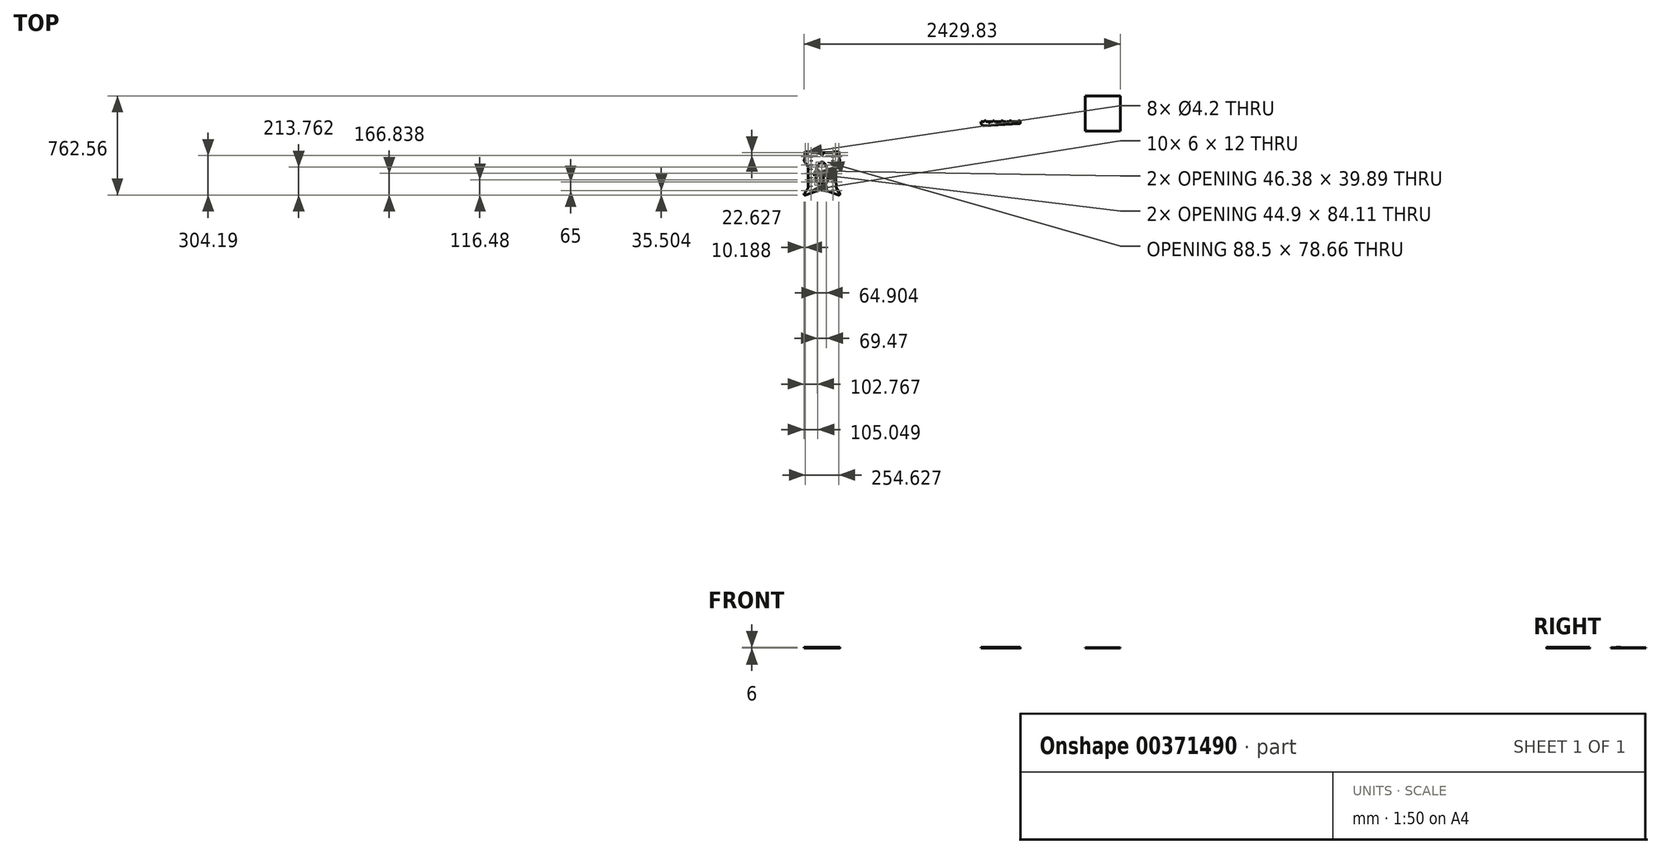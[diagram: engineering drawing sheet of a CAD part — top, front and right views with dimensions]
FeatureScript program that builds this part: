
annotation { "Feature Type Name" : "Feature", "Feature Type Description" : "" }
export const myFeature = defineFeature(function(context is Context, id is Id, definition is map)
    precondition{}
    {
        {
            var Q0;
            Q0=qCreatedBy(makeId("Top.planeOp"),FACE);
            var sketch = newSketch(context, id + "F0", { "sketchPlane" : qUnion([Q0])});
            skCircle(sketch, "E0", {"center": v(-43.53, 80.15) * mm, "radius": 6.15 * mm});
            skCircle(sketch, "E1", {"center": v(72.47, 79.15) * mm, "radius": 5.05 * mm});
            skLineSegment(sketch, "E2.bottom", {"start": v(-57.57, 96.15) * mm, "end": v(-15.53, 96.15) * mm});
            skLineSegment(sketch, "E2.left", {"start": v(-59.57, 94.15) * mm, "end": v(-59.57, 62.7) * mm});
            skLineSegment(sketch, "E2.right", {"start": v(204.43, 94.15) * mm, "end": v(204.43, 62.7) * mm});
            skCircle(sketch, "E3", {"center": v(-32.22, 91.47) * mm, "radius": 2.1 * mm});
            skCircle(sketch, "E4", {"center": v(-54.84, 91.47) * mm, "radius": 2.1 * mm});
            skCircle(sketch, "E5", {"center": v(-54.84, 68.84) * mm, "radius": 2.1 * mm});
            skCircle(sketch, "E6", {"center": v(-32.22, 68.84) * mm, "radius": 2.1 * mm});
            skCircle(sketch, "E7.1.0.0", {"center": v(188.47, 80.15) * mm, "radius": 6.15 * mm});
            skCircle(sketch, "E7.1.0.1", {"center": v(199.78, 91.47) * mm, "radius": 2.1 * mm});
            skCircle(sketch, "E7.1.0.2", {"center": v(177.16, 91.47) * mm, "radius": 2.1 * mm});
            skCircle(sketch, "E7.1.0.3", {"center": v(177.16, 68.84) * mm, "radius": 2.1 * mm});
            skCircle(sketch, "E7.1.0.4", {"center": v(199.78, 68.84) * mm, "radius": 2.1 * mm});
            skLineSegment(sketch, "E7.direction1", {"start": v(-43.53, 80.15) * mm, "end": v(188.47, 80.15) * mm, "construction": true});
            skCircle(sketch, "E8", {"center": v(72.47, 71.15) * mm, "radius": 1.65 * mm});
            skCircle(sketch, "E9", {"center": v(80.47, 79.15) * mm, "radius": 1.65 * mm});
            skCircle(sketch, "E10", {"center": v(72.47, 87.15) * mm, "radius": 1.65 * mm});
            skCircle(sketch, "E11", {"center": v(64.47, 79.15) * mm, "radius": 1.65 * mm});
            skLineSegment(sketch, "E12.bottom", {"start": v(-13.53, 86.15) * mm, "end": v(-7.53, 86.15) * mm});
            skLineSegment(sketch, "E12.top", {"start": v(-13.53, 74.15) * mm, "end": v(-7.53, 74.15) * mm});
            skLineSegment(sketch, "E12.left", {"start": v(-13.53, 86.15) * mm, "end": v(-13.53, 74.15) * mm});
            skLineSegment(sketch, "E12.right", {"start": v(-7.53, 86.15) * mm, "end": v(-7.53, 74.15) * mm});
            skLineSegment(sketch, "E13.0.1.0", {"start": v(-13.53, 21.15) * mm, "end": v(-7.53, 21.15) * mm});
            skLineSegment(sketch, "E13.0.1.1", {"start": v(-13.53, 21.15) * mm, "end": v(-13.53, 9.15) * mm});
            skLineSegment(sketch, "E13.0.1.2", {"start": v(-13.53, 9.15) * mm, "end": v(-7.53, 9.15) * mm});
            skLineSegment(sketch, "E13.0.1.3", {"start": v(-7.53, 21.15) * mm, "end": v(-7.53, 9.15) * mm});
            skLineSegment(sketch, "E13.0.2.0", {"start": v(-13.53, -43.85) * mm, "end": v(-7.53, -43.85) * mm});
            skLineSegment(sketch, "E13.0.2.1", {"start": v(-13.53, -43.85) * mm, "end": v(-13.53, -55.85) * mm});
            skLineSegment(sketch, "E13.0.2.2", {"start": v(-13.53, -55.85) * mm, "end": v(-7.53, -55.85) * mm});
            skLineSegment(sketch, "E13.0.2.3", {"start": v(-7.53, -43.85) * mm, "end": v(-7.53, -55.85) * mm});
            skLineSegment(sketch, "E13.0.3.0", {"start": v(-13.53, -108.85) * mm, "end": v(-7.53, -108.85) * mm});
            skLineSegment(sketch, "E13.0.3.1", {"start": v(-13.53, -108.85) * mm, "end": v(-13.53, -120.85) * mm});
            skLineSegment(sketch, "E13.0.3.2", {"start": v(-13.53, -120.85) * mm, "end": v(-7.53, -120.85) * mm});
            skLineSegment(sketch, "E13.0.3.3", {"start": v(-7.53, -108.85) * mm, "end": v(-7.53, -120.85) * mm});
            skLineSegment(sketch, "E13.1.0.0", {"start": v(152.47, 86.15) * mm, "end": v(158.47, 86.15) * mm});
            skLineSegment(sketch, "E13.1.0.1", {"start": v(152.47, 86.15) * mm, "end": v(152.47, 74.15) * mm});
            skLineSegment(sketch, "E13.1.0.2", {"start": v(152.47, 74.15) * mm, "end": v(158.47, 74.15) * mm});
            skLineSegment(sketch, "E13.1.0.3", {"start": v(158.47, 86.15) * mm, "end": v(158.47, 74.15) * mm});
            skLineSegment(sketch, "E13.1.1.0", {"start": v(152.47, 21.15) * mm, "end": v(158.47, 21.15) * mm});
            skLineSegment(sketch, "E13.1.1.1", {"start": v(152.47, 21.15) * mm, "end": v(152.47, 9.15) * mm});
            skLineSegment(sketch, "E13.1.1.2", {"start": v(152.47, 9.15) * mm, "end": v(158.47, 9.15) * mm});
            skLineSegment(sketch, "E13.1.1.3", {"start": v(158.47, 21.15) * mm, "end": v(158.47, 9.15) * mm});
            skLineSegment(sketch, "E13.1.2.0", {"start": v(152.47, -43.85) * mm, "end": v(158.47, -43.85) * mm});
            skLineSegment(sketch, "E13.1.2.1", {"start": v(152.47, -43.85) * mm, "end": v(152.47, -55.85) * mm});
            skLineSegment(sketch, "E13.1.2.2", {"start": v(152.47, -55.85) * mm, "end": v(158.47, -55.85) * mm});
            skLineSegment(sketch, "E13.1.2.3", {"start": v(158.47, -43.85) * mm, "end": v(158.47, -55.85) * mm});
            skLineSegment(sketch, "E13.1.3.0", {"start": v(152.47, -108.85) * mm, "end": v(158.47, -108.85) * mm});
            skLineSegment(sketch, "E13.1.3.1", {"start": v(152.47, -108.85) * mm, "end": v(152.47, -120.85) * mm});
            skLineSegment(sketch, "E13.1.3.2", {"start": v(152.47, -120.85) * mm, "end": v(158.47, -120.85) * mm});
            skLineSegment(sketch, "E13.1.3.3", {"start": v(158.47, -108.85) * mm, "end": v(158.47, -120.85) * mm});
            skLineSegment(sketch, "E13.direction1", {"start": v(-13.53, 86.15) * mm, "end": v(152.47, 86.15) * mm, "construction": true});
            skLineSegment(sketch, "E13.direction2", {"start": v(-13.53, 86.15) * mm, "end": v(-13.53, 21.15) * mm, "construction": true});
            skCircle(sketch, "E14", {"center": v(-10.53, 47.65) * mm, "radius": 2 * mm});
            skPoint(sketch, "E14.centerSnap0", {"position": v(-10.53, 74.15) * mm});
            skCircle(sketch, "E15.0.1.0", {"center": v(-10.53, -17.35) * mm, "radius": 2 * mm});
            skCircle(sketch, "E15.0.2.0", {"center": v(-10.53, -82.35) * mm, "radius": 2 * mm});
            skCircle(sketch, "E15.1.0.0", {"center": v(155.47, 47.65) * mm, "radius": 2 * mm});
            skCircle(sketch, "E15.1.1.0", {"center": v(155.47, -17.35) * mm, "radius": 2 * mm});
            skCircle(sketch, "E15.1.2.0", {"center": v(155.47, -82.35) * mm, "radius": 2 * mm});
            skLineSegment(sketch, "E15.direction1", {"start": v(-10.53, 47.65) * mm, "end": v(155.47, 47.65) * mm, "construction": true});
            skLineSegment(sketch, "E15.direction2", {"start": v(-10.53, 47.65) * mm, "end": v(-10.53, -17.35) * mm, "construction": true});
            skArc(sketch, "E16", {"start": v(23.68, -28.57) * mm, "mid": v(15.8, -47.74) * mm, "end": v(15.16, -68.46) * mm});
            skPoint(sketch, "E16.centerSnap0", {"position": v(72.47, 47.65) * mm});
            skArc(sketch, "E17", {"start": v(95.76, 21.5) * mm, "mid": v(72.47, 37.74) * mm, "end": v(49.18, 21.5) * mm});
            skArc(sketch, "E18", {"start": v(38.9, -121.45) * mm, "mid": v(48.6, -133.7) * mm, "end": v(62.47, -140.92) * mm});
            skLineSegment(sketch, "E19", {"start": v(17.57, -78.4) * mm, "end": v(38.9, -121.45) * mm});
            skLineSegment(sketch, "E20", {"start": v(106.05, -121.45) * mm, "end": v(127.37, -78.4) * mm});
            skArc(sketch, "E21.trimOffspring", {"start": v(129.78, -68.46) * mm, "mid": v(129.14, -47.74) * mm, "end": v(121.26, -28.57) * mm});
            skLineSegment(sketch, "E22", {"start": v(28.22, -19.65) * mm, "end": v(49.18, 21.5) * mm});
            skLineSegment(sketch, "E23", {"start": v(95.76, 21.5) * mm, "end": v(116.72, -19.65) * mm});
            skLineSegment(sketch, "E24.top", {"start": v(-11.53, 91.15) * mm, "end": v(156.47, 91.15) * mm});
            skLineSegment(sketch, "E24.left", {"start": v(-13.53, 94.15) * mm, "end": v(-13.53, 93.15) * mm});
            skLineSegment(sketch, "E24.right", {"start": v(158.47, 94.15) * mm, "end": v(158.47, 93.15) * mm});
            skLineSegment(sketch, "E25.trimOffspring", {"start": v(160.47, 96.15) * mm, "end": v(202.43, 96.15) * mm});
            skPoint(sketch, "E26.visualSharp", {"position": v(-13.53, 96.15) * mm});
            skArc(sketch, "E26.filletArc", {"start": v(-13.53, 94.15) * mm, "mid": v(-14.12, 95.57) * mm, "end": v(-15.53, 96.15) * mm});
            skPoint(sketch, "E27.visualSharp", {"position": v(-13.53, 91.15) * mm});
            skArc(sketch, "E27.filletArc", {"start": v(-13.53, 93.15) * mm, "mid": v(-12.94, 91.74) * mm, "end": v(-11.53, 91.15) * mm});
            skPoint(sketch, "E28.visualSharp", {"position": v(158.47, 96.15) * mm});
            skArc(sketch, "E28.filletArc", {"start": v(160.47, 96.15) * mm, "mid": v(159.06, 95.57) * mm, "end": v(158.47, 94.15) * mm});
            skPoint(sketch, "E29.visualSharp", {"position": v(158.47, 91.15) * mm});
            skArc(sketch, "E29.filletArc", {"start": v(156.47, 91.15) * mm, "mid": v(157.88, 91.74) * mm, "end": v(158.47, 93.15) * mm});
            skPoint(sketch, "E30.visualSharp", {"position": v(204.43, 96.15) * mm});
            skArc(sketch, "E30.filletArc", {"start": v(204.43, 94.15) * mm, "mid": v(203.84, 95.57) * mm, "end": v(202.43, 96.15) * mm});
            skPoint(sketch, "E31.visualSharp", {"position": v(-59.57, 96.15) * mm});
            skArc(sketch, "E31.filletArc", {"start": v(-57.57, 96.15) * mm, "mid": v(-58.98, 95.57) * mm, "end": v(-59.57, 94.15) * mm});
            skCircle(sketch, "E32", {"center": v(-57.53, -207.85) * mm, "radius": 2.5 * mm});
            skPoint(sketch, "E32.centerSnap0", {"position": v(-10.53, -120.85) * mm});
            skCircle(sketch, "E33", {"center": v(202.47, -207.85) * mm, "radius": 2.5 * mm});
            skCircle(sketch, "E34", {"center": v(-57.53, 52.15) * mm, "radius": 2.5 * mm});
            skCircle(sketch, "E35", {"center": v(202.47, 52.15) * mm, "radius": 2.5 * mm});
            skArc(sketch, "E36", {"start": v(208.74, 48.03) * mm, "mid": v(209.97, 52.18) * mm, "end": v(208.7, 56.33) * mm});
            skLineSegment(sketch, "E37", {"start": v(204.43, 62.7) * mm, "end": v(208.7, 56.33) * mm});
            skArc(sketch, "E38", {"start": v(-63.53, -203.35) * mm, "mid": v(-63.6, -212.27) * mm, "end": v(-55.09, -214.94) * mm});
            skArc(sketch, "E39", {"start": v(200.03, -214.94) * mm, "mid": v(208.35, -212.5) * mm, "end": v(208.8, -203.84) * mm});
            skArc(sketch, "E40", {"start": v(-63.8, 56.27) * mm, "mid": v(-65.03, 52.15) * mm, "end": v(-63.8, 48.03) * mm});
            skLineSegment(sketch, "E41", {"start": v(-59.57, 62.7) * mm, "end": v(-63.8, 56.27) * mm});
            skLineSegment(sketch, "E42", {"start": v(-63.8, 48.03) * mm, "end": v(-38.8, 10) * mm});
            skLineSegment(sketch, "E43", {"start": v(-32.22, -11.97) * mm, "end": v(-32.22, -148.25) * mm});
            skLineSegment(sketch, "E44", {"start": v(-40.21, -172.24) * mm, "end": v(-63.8, -203.7) * mm});
            skLineSegment(sketch, "E45", {"start": v(208.74, 48.03) * mm, "end": v(184.1, 10.56) * mm});
            skLineSegment(sketch, "E46", {"start": v(177.54, -12.63) * mm, "end": v(182.09, -161.58) * mm});
            skLineSegment(sketch, "E47", {"start": v(182.09, -161.58) * mm, "end": v(208.8, -203.84) * mm});
            skLineSegment(sketch, "E48", {"start": v(-55.09, -214.94) * mm, "end": v(59.43, -175.45) * mm});
            skLineSegment(sketch, "E49", {"start": v(85.5, -175.45) * mm, "end": v(200.03, -214.94) * mm});
            skLineSegment(sketch, "E50", {"start": v(23.68, -28.57) * mm, "end": v(60.93, -46.47) * mm});
            skLineSegment(sketch, "E51", {"start": v(17.57, -78.4) * mm, "end": v(62.47, -56.82) * mm});
            skLineSegment(sketch, "E52", {"start": v(28.22, -19.65) * mm, "end": v(72.47, -40.92) * mm});
            skLineSegment(sketch, "E53", {"start": v(116.72, -19.65) * mm, "end": v(72.47, -40.92) * mm});
            skLineSegment(sketch, "E54.trimOffspring", {"start": v(84.01, -46.47) * mm, "end": v(129.78, -68.46) * mm});
            skLineSegment(sketch, "E55.trimOffspring", {"start": v(60.93, -46.47) * mm, "end": v(15.16, -68.46) * mm});
            skLineSegment(sketch, "E56.trimOffspring", {"start": v(82.47, -56.82) * mm, "end": v(127.37, -78.4) * mm});
            skLineSegment(sketch, "E57.trimOffspring", {"start": v(84.01, -46.47) * mm, "end": v(121.26, -28.57) * mm});
            skLineSegment(sketch, "E58.left", {"start": v(62.47, -56.82) * mm, "end": v(62.47, -140.92) * mm});
            skLineSegment(sketch, "E58.right", {"start": v(82.47, -56.82) * mm, "end": v(82.47, -140.92) * mm});
            skLineSegment(sketch, "E59.0.0.4", {"start": v(-13.53, -173.85) * mm, "end": v(-7.53, -173.85) * mm});
            skLineSegment(sketch, "E59.3.0.4", {"start": v(-13.53, -173.85) * mm, "end": v(-13.53, -185.85) * mm});
            skLineSegment(sketch, "E59.6.0.4", {"start": v(-13.53, -185.85) * mm, "end": v(-7.53, -185.85) * mm});
            skLineSegment(sketch, "E59.9.0.4", {"start": v(-7.53, -173.85) * mm, "end": v(-7.53, -185.85) * mm});
            skLineSegment(sketch, "E59.0.1.4", {"start": v(152.47, -173.85) * mm, "end": v(158.47, -173.85) * mm});
            skLineSegment(sketch, "E59.3.1.4", {"start": v(152.47, -173.85) * mm, "end": v(152.47, -185.85) * mm});
            skLineSegment(sketch, "E59.6.1.4", {"start": v(152.47, -185.85) * mm, "end": v(158.47, -185.85) * mm});
            skLineSegment(sketch, "E59.9.1.4", {"start": v(158.47, -173.85) * mm, "end": v(158.47, -185.85) * mm});
            skCircle(sketch, "E60.0.0.3", {"center": v(-10.53, -147.35) * mm, "radius": 2 * mm});
            skCircle(sketch, "E60.0.1.3", {"center": v(155.47, -147.35) * mm, "radius": 2 * mm});
            skPoint(sketch, "E61.orphan", {"position": v(72.47, -52.01) * mm});
            skArc(sketch, "E62.trimOffspring", {"start": v(82.47, -140.92) * mm, "mid": v(96.33, -133.7) * mm, "end": v(106.05, -121.45) * mm});
            skPoint(sketch, "E63.visualSharp", {"position": v(72.47, -170.96) * mm});
            skArc(sketch, "E63.filletArc", {"start": v(85.5, -175.45) * mm, "mid": v(72.47, -173.27) * mm, "end": v(59.43, -175.45) * mm});
            skPoint(sketch, "E64.visualSharp", {"position": v(-32.22, -161.58) * mm});
            skArc(sketch, "E64.filletArc", {"start": v(-40.21, -172.24) * mm, "mid": v(-34.27, -160.9) * mm, "end": v(-32.22, -148.25) * mm});
            skPoint(sketch, "E65.visualSharp", {"position": v(177.16, 0) * mm});
            skArc(sketch, "E65.filletArc", {"start": v(184.1, 10.56) * mm, "mid": v(179.03, -0.53) * mm, "end": v(177.54, -12.63) * mm});
            skPoint(sketch, "E66.visualSharp", {"position": v(-32.22, 0) * mm});
            skArc(sketch, "E66.filletArc", {"start": v(-32.22, -11.97) * mm, "mid": v(-33.9, -0.5) * mm, "end": v(-38.8, 10) * mm});
            skLineSegment(sketch, "E67.top", {"start": v(-1752.05, -335.9) * mm, "end": v(-1746.05, -335.9) * mm});
            skLineSegment(sketch, "E67.right", {"start": v(-1746.05, -323.9) * mm, "end": v(-1746.05, -335.9) * mm});
            skLineSegment(sketch, "E68.0.1.0", {"start": v(-1752.05, -388.9) * mm, "end": v(-1746.05, -388.9) * mm});
            skLineSegment(sketch, "E68.0.1.1", {"start": v(-1752.05, -388.9) * mm, "end": v(-1752.05, -400.9) * mm});
            skLineSegment(sketch, "E68.0.1.2", {"start": v(-1752.05, -400.9) * mm, "end": v(-1746.05, -400.9) * mm});
            skLineSegment(sketch, "E68.0.1.3", {"start": v(-1746.05, -388.9) * mm, "end": v(-1746.05, -400.9) * mm});
            skLineSegment(sketch, "E68.0.2.0", {"start": v(-1752.05, -453.9) * mm, "end": v(-1746.05, -453.9) * mm});
            skLineSegment(sketch, "E68.0.2.1", {"start": v(-1752.05, -453.9) * mm, "end": v(-1752.05, -465.9) * mm});
            skLineSegment(sketch, "E68.0.2.2", {"start": v(-1752.05, -465.9) * mm, "end": v(-1746.05, -465.9) * mm});
            skLineSegment(sketch, "E68.0.2.3", {"start": v(-1746.05, -453.9) * mm, "end": v(-1746.05, -465.9) * mm});
            skLineSegment(sketch, "E68.0.3.0", {"start": v(-1752.05, -518.9) * mm, "end": v(-1746.05, -518.9) * mm});
            skLineSegment(sketch, "E68.0.3.1", {"start": v(-1752.05, -518.9) * mm, "end": v(-1752.05, -530.9) * mm});
            skLineSegment(sketch, "E68.0.3.2", {"start": v(-1752.05, -530.9) * mm, "end": v(-1746.05, -530.9) * mm});
            skLineSegment(sketch, "E68.0.3.3", {"start": v(-1746.05, -518.9) * mm, "end": v(-1746.05, -530.9) * mm});
            skLineSegment(sketch, "E68.1.0.1", {"start": v(-1586.05, -323.9) * mm, "end": v(-1586.05, -335.9) * mm});
            skLineSegment(sketch, "E68.1.0.3", {"start": v(-1580.05, -323.9) * mm, "end": v(-1580.05, -335.9) * mm});
            skLineSegment(sketch, "E68.1.1.0", {"start": v(-1586.05, -388.9) * mm, "end": v(-1580.05, -388.9) * mm});
            skLineSegment(sketch, "E68.1.1.1", {"start": v(-1586.05, -388.9) * mm, "end": v(-1586.05, -400.9) * mm});
            skLineSegment(sketch, "E68.1.1.2", {"start": v(-1586.05, -400.9) * mm, "end": v(-1580.05, -400.9) * mm});
            skLineSegment(sketch, "E68.1.1.3", {"start": v(-1580.05, -388.9) * mm, "end": v(-1580.05, -400.9) * mm});
            skLineSegment(sketch, "E68.1.2.0", {"start": v(-1586.05, -453.9) * mm, "end": v(-1580.05, -453.9) * mm});
            skLineSegment(sketch, "E68.1.2.1", {"start": v(-1586.05, -453.9) * mm, "end": v(-1586.05, -465.9) * mm});
            skLineSegment(sketch, "E68.1.2.2", {"start": v(-1586.05, -465.9) * mm, "end": v(-1580.05, -465.9) * mm});
            skLineSegment(sketch, "E68.1.2.3", {"start": v(-1580.05, -453.9) * mm, "end": v(-1580.05, -465.9) * mm});
            skLineSegment(sketch, "E68.1.3.0", {"start": v(-1586.05, -518.9) * mm, "end": v(-1580.05, -518.9) * mm});
            skLineSegment(sketch, "E68.1.3.1", {"start": v(-1586.05, -518.9) * mm, "end": v(-1586.05, -530.9) * mm});
            skLineSegment(sketch, "E68.1.3.2", {"start": v(-1586.05, -530.9) * mm, "end": v(-1580.05, -530.9) * mm});
            skLineSegment(sketch, "E68.1.3.3", {"start": v(-1580.05, -518.9) * mm, "end": v(-1580.05, -530.9) * mm});
            skLineSegment(sketch, "E68.direction1", {"start": v(-1752.05, -323.9) * mm, "end": v(-1586.05, -323.9) * mm, "construction": true});
            skLineSegment(sketch, "E68.direction2", {"start": v(-1752.05, -323.9) * mm, "end": v(-1752.05, -388.9) * mm, "construction": true});
            skCircle(sketch, "E69", {"center": v(-1749.05, -362.4) * mm, "radius": 2 * mm});
            skPoint(sketch, "E69.centerSnap0", {"position": v(-1749.05, -335.9) * mm});
            skCircle(sketch, "E70.0.1.0", {"center": v(-1749.05, -427.4) * mm, "radius": 2 * mm});
            skCircle(sketch, "E70.0.2.0", {"center": v(-1749.05, -492.4) * mm, "radius": 2 * mm});
            skCircle(sketch, "E70.1.0.0", {"center": v(-1583.05, -362.4) * mm, "radius": 2 * mm});
            skCircle(sketch, "E70.1.1.0", {"center": v(-1583.05, -427.4) * mm, "radius": 2 * mm});
            skCircle(sketch, "E70.1.2.0", {"center": v(-1583.05, -492.4) * mm, "radius": 2 * mm});
            skLineSegment(sketch, "E70.direction1", {"start": v(-1749.05, -362.4) * mm, "end": v(-1583.05, -362.4) * mm, "construction": true});
            skLineSegment(sketch, "E70.direction2", {"start": v(-1749.05, -362.4) * mm, "end": v(-1749.05, -427.4) * mm, "construction": true});
            skArc(sketch, "E71", {"start": v(-1714.83, -438.62) * mm, "mid": v(-1722.72, -457.79) * mm, "end": v(-1723.36, -478.5) * mm});
            skPoint(sketch, "E71.centerSnap0", {"position": v(-1666.05, -362.4) * mm});
            skArc(sketch, "E72", {"start": v(-1642.76, -388.55) * mm, "mid": v(-1666.05, -372.3) * mm, "end": v(-1689.34, -388.55) * mm});
            skArc(sketch, "E73", {"start": v(-1699.62, -531.5) * mm, "mid": v(-1689.91, -543.75) * mm, "end": v(-1676.05, -550.97) * mm});
            skLineSegment(sketch, "E74", {"start": v(-1720.95, -488.45) * mm, "end": v(-1699.62, -531.5) * mm});
            skLineSegment(sketch, "E75", {"start": v(-1632.47, -531.5) * mm, "end": v(-1611.14, -488.45) * mm});
            skArc(sketch, "E76.trimOffspring", {"start": v(-1608.74, -478.5) * mm, "mid": v(-1609.37, -457.79) * mm, "end": v(-1617.26, -438.62) * mm});
            skLineSegment(sketch, "E77", {"start": v(-1710.3, -429.7) * mm, "end": v(-1689.34, -388.55) * mm});
            skLineSegment(sketch, "E78", {"start": v(-1642.76, -388.55) * mm, "end": v(-1621.8, -429.7) * mm});
            skCircle(sketch, "E79", {"center": v(-1796.05, -617.9) * mm, "radius": 2.5 * mm});
            skPoint(sketch, "E79.centerSnap0", {"position": v(-1749.05, -530.9) * mm});
            skCircle(sketch, "E80", {"center": v(-1536.05, -617.9) * mm, "radius": 2.5 * mm});
            skCircle(sketch, "E81", {"center": v(-1796.05, -357.9) * mm, "radius": 2.5 * mm});
            skCircle(sketch, "E82", {"center": v(-1536.05, -357.9) * mm, "radius": 2.5 * mm});
            skArc(sketch, "E83", {"start": v(-1529.78, -362.02) * mm, "mid": v(-1528.55, -357.86) * mm, "end": v(-1529.82, -353.72) * mm});
            skLineSegment(sketch, "E84", {"start": v(-1534.09, -347.35) * mm, "end": v(-1529.82, -353.72) * mm});
            skArc(sketch, "E85", {"start": v(-1802.05, -613.4) * mm, "mid": v(-1802.1, -622.31) * mm, "end": v(-1793.6, -624.99) * mm});
            skArc(sketch, "E86", {"start": v(-1538.5, -624.99) * mm, "mid": v(-1530.17, -622.55) * mm, "end": v(-1529.7, -613.89) * mm});
            skArc(sketch, "E87", {"start": v(-1802.32, -353.78) * mm, "mid": v(-1803.55, -357.9) * mm, "end": v(-1802.32, -362.02) * mm});
            skLineSegment(sketch, "E88", {"start": v(-1798.09, -347.35) * mm, "end": v(-1802.32, -353.78) * mm});
            skLineSegment(sketch, "E89", {"start": v(-1802.32, -362.02) * mm, "end": v(-1777.31, -400.04) * mm});
            skLineSegment(sketch, "E90", {"start": v(-1770.73, -422.02) * mm, "end": v(-1770.73, -558.3) * mm});
            skLineSegment(sketch, "E91", {"start": v(-1778.73, -582.3) * mm, "end": v(-1802.32, -613.75) * mm});
            skLineSegment(sketch, "E92", {"start": v(-1529.78, -362.02) * mm, "end": v(-1554.42, -399.49) * mm});
            skLineSegment(sketch, "E93", {"start": v(-1560.98, -422.68) * mm, "end": v(-1556.43, -571.63) * mm});
            skLineSegment(sketch, "E94", {"start": v(-1556.43, -571.63) * mm, "end": v(-1529.7, -613.89) * mm});
            skLineSegment(sketch, "E95", {"start": v(-1793.6, -624.99) * mm, "end": v(-1679.09, -585.5) * mm});
            skLineSegment(sketch, "E96", {"start": v(-1653, -585.5) * mm, "end": v(-1538.5, -624.99) * mm});
            skLineSegment(sketch, "E97", {"start": v(-1714.83, -438.62) * mm, "end": v(-1677.6, -456.51) * mm});
            skLineSegment(sketch, "E98", {"start": v(-1720.95, -488.45) * mm, "end": v(-1676.05, -466.87) * mm});
            skLineSegment(sketch, "E99", {"start": v(-1710.3, -429.7) * mm, "end": v(-1666.05, -450.97) * mm});
            skLineSegment(sketch, "E100", {"start": v(-1621.8, -429.7) * mm, "end": v(-1666.05, -450.97) * mm});
            skLineSegment(sketch, "E101.trimOffspring", {"start": v(-1654.5, -456.51) * mm, "end": v(-1608.74, -478.5) * mm});
            skLineSegment(sketch, "E102.trimOffspring", {"start": v(-1677.6, -456.51) * mm, "end": v(-1723.36, -478.5) * mm});
            skLineSegment(sketch, "E103.trimOffspring", {"start": v(-1656.05, -466.87) * mm, "end": v(-1611.14, -488.45) * mm});
            skLineSegment(sketch, "E104.trimOffspring", {"start": v(-1654.5, -456.51) * mm, "end": v(-1617.26, -438.62) * mm});
            skLineSegment(sketch, "E105.left", {"start": v(-1676.05, -466.87) * mm, "end": v(-1676.05, -550.97) * mm});
            skLineSegment(sketch, "E105.right", {"start": v(-1656.05, -466.87) * mm, "end": v(-1656.05, -550.97) * mm});
            skLineSegment(sketch, "E106.0.0.4", {"start": v(-1752.05, -583.9) * mm, "end": v(-1746.05, -583.9) * mm});
            skLineSegment(sketch, "E106.3.0.4", {"start": v(-1752.05, -583.9) * mm, "end": v(-1752.05, -595.9) * mm});
            skLineSegment(sketch, "E106.6.0.4", {"start": v(-1752.05, -595.9) * mm, "end": v(-1746.05, -595.9) * mm});
            skLineSegment(sketch, "E106.9.0.4", {"start": v(-1746.05, -583.9) * mm, "end": v(-1746.05, -595.9) * mm});
            skLineSegment(sketch, "E106.0.1.4", {"start": v(-1586.05, -583.9) * mm, "end": v(-1580.05, -583.9) * mm});
            skLineSegment(sketch, "E106.3.1.4", {"start": v(-1586.05, -583.9) * mm, "end": v(-1586.05, -595.9) * mm});
            skLineSegment(sketch, "E106.6.1.4", {"start": v(-1586.05, -595.9) * mm, "end": v(-1580.05, -595.9) * mm});
            skLineSegment(sketch, "E106.9.1.4", {"start": v(-1580.05, -583.9) * mm, "end": v(-1580.05, -595.9) * mm});
            skCircle(sketch, "E107.0.0.3", {"center": v(-1749.05, -557.4) * mm, "radius": 2 * mm});
            skCircle(sketch, "E107.0.1.3", {"center": v(-1583.05, -557.4) * mm, "radius": 2 * mm});
            skPoint(sketch, "E108.orphan", {"position": v(-1666.05, -462.06) * mm});
            skArc(sketch, "E109.trimOffspring", {"start": v(-1656.05, -550.97) * mm, "mid": v(-1642.18, -543.75) * mm, "end": v(-1632.47, -531.5) * mm});
            skPoint(sketch, "E110.visualSharp", {"position": v(-1666.05, -581) * mm});
            skArc(sketch, "E110.filletArc", {"start": v(-1653, -585.5) * mm, "mid": v(-1666.05, -583.32) * mm, "end": v(-1679.09, -585.5) * mm});
            skPoint(sketch, "E111.visualSharp", {"position": v(-1770.73, -571.63) * mm});
            skArc(sketch, "E111.filletArc", {"start": v(-1778.73, -582.3) * mm, "mid": v(-1772.79, -570.94) * mm, "end": v(-1770.73, -558.3) * mm});
            skPoint(sketch, "E112.visualSharp", {"position": v(-1561.36, -410.05) * mm});
            skArc(sketch, "E112.filletArc", {"start": v(-1554.42, -399.49) * mm, "mid": v(-1559.49, -410.58) * mm, "end": v(-1560.98, -422.68) * mm});
            skPoint(sketch, "E113.visualSharp", {"position": v(-1770.73, -410.05) * mm});
            skArc(sketch, "E113.filletArc", {"start": v(-1770.73, -422.02) * mm, "mid": v(-1772.41, -410.55) * mm, "end": v(-1777.31, -400.04) * mm});
            skLineSegment(sketch, "E114", {"start": v(-1586.05, -323.9) * mm, "end": v(-1580.05, -323.9) * mm});
            skLineSegment(sketch, "E115", {"start": v(-1580.05, -335.9) * mm, "end": v(-1586.05, -335.9) * mm});
            skLineSegment(sketch, "E116", {"start": v(-1798.09, -347.35) * mm, "end": v(-1798.09, -327.35) * mm});
            skLineSegment(sketch, "E117", {"start": v(-1534.09, -327.35) * mm, "end": v(-1534.09, -347.35) * mm});
            skCircle(sketch, "E118", {"center": v(-1782.05, -309.9) * mm, "radius": 6.15 * mm});
            skCircle(sketch, "E119", {"center": v(-1666.05, -310.9) * mm, "radius": 5.05 * mm});
            skLineSegment(sketch, "E120.bottom", {"start": v(-1796.09, -293.9) * mm, "end": v(-1754.05, -293.9) * mm});
            skLineSegment(sketch, "E120.left", {"start": v(-1798.09, -295.9) * mm, "end": v(-1798.09, -327.35) * mm});
            skLineSegment(sketch, "E120.right", {"start": v(-1534.09, -295.9) * mm, "end": v(-1534.09, -327.35) * mm});
            skCircle(sketch, "E121", {"center": v(-1770.73, -298.58) * mm, "radius": 2.1 * mm});
            skCircle(sketch, "E122", {"center": v(-1793.36, -298.58) * mm, "radius": 2.1 * mm});
            skCircle(sketch, "E123", {"center": v(-1793.36, -321.2) * mm, "radius": 2.1 * mm});
            skCircle(sketch, "E124", {"center": v(-1770.73, -321.2) * mm, "radius": 2.1 * mm});
            skCircle(sketch, "E125.1.0.0", {"center": v(-1550.05, -309.9) * mm, "radius": 6.15 * mm});
            skCircle(sketch, "E125.1.0.1", {"center": v(-1538.73, -298.58) * mm, "radius": 2.1 * mm});
            skCircle(sketch, "E125.1.0.2", {"center": v(-1561.36, -298.58) * mm, "radius": 2.1 * mm});
            skCircle(sketch, "E125.1.0.3", {"center": v(-1561.36, -321.2) * mm, "radius": 2.1 * mm});
            skCircle(sketch, "E125.1.0.4", {"center": v(-1538.73, -321.2) * mm, "radius": 2.1 * mm});
            skLineSegment(sketch, "E125.direction1", {"start": v(-1782.05, -309.9) * mm, "end": v(-1550.05, -309.9) * mm, "construction": true});
            skCircle(sketch, "E126", {"center": v(-1666.05, -318.9) * mm, "radius": 1.65 * mm});
            skCircle(sketch, "E127", {"center": v(-1658.05, -310.9) * mm, "radius": 1.65 * mm});
            skCircle(sketch, "E128", {"center": v(-1666.05, -302.9) * mm, "radius": 1.65 * mm});
            skCircle(sketch, "E129", {"center": v(-1674.05, -310.9) * mm, "radius": 1.65 * mm});
            skLineSegment(sketch, "E130.top", {"start": v(-1750.05, -298.9) * mm, "end": v(-1582.05, -298.9) * mm});
            skLineSegment(sketch, "E130.left", {"start": v(-1752.05, -295.9) * mm, "end": v(-1752.05, -296.9) * mm});
            skLineSegment(sketch, "E130.right", {"start": v(-1580.05, -295.9) * mm, "end": v(-1580.05, -296.9) * mm});
            skLineSegment(sketch, "E131.trimOffspring", {"start": v(-1578.05, -293.9) * mm, "end": v(-1536.09, -293.9) * mm});
            skPoint(sketch, "E132.visualSharp", {"position": v(-1752.05, -293.9) * mm});
            skArc(sketch, "E132.filletArc", {"start": v(-1752.05, -295.9) * mm, "mid": v(-1752.63, -294.48) * mm, "end": v(-1754.05, -293.9) * mm});
            skPoint(sketch, "E133.visualSharp", {"position": v(-1752.05, -298.9) * mm});
            skArc(sketch, "E133.filletArc", {"start": v(-1752.05, -296.9) * mm, "mid": v(-1751.46, -298.31) * mm, "end": v(-1750.05, -298.9) * mm});
            skPoint(sketch, "E134.visualSharp", {"position": v(-1580.05, -293.9) * mm});
            skArc(sketch, "E134.filletArc", {"start": v(-1578.05, -293.9) * mm, "mid": v(-1579.46, -294.48) * mm, "end": v(-1580.05, -295.9) * mm});
            skPoint(sketch, "E135.visualSharp", {"position": v(-1580.05, -298.9) * mm});
            skArc(sketch, "E135.filletArc", {"start": v(-1582.05, -298.9) * mm, "mid": v(-1580.63, -298.31) * mm, "end": v(-1580.05, -296.9) * mm});
            skPoint(sketch, "E136.visualSharp", {"position": v(-1534.09, -293.9) * mm});
            skArc(sketch, "E136.filletArc", {"start": v(-1534.09, -295.9) * mm, "mid": v(-1534.67, -294.48) * mm, "end": v(-1536.09, -293.9) * mm});
            skPoint(sketch, "E137.visualSharp", {"position": v(-1798.09, -293.9) * mm});
            skArc(sketch, "E137.filletArc", {"start": v(-1796.09, -293.9) * mm, "mid": v(-1797.5, -294.48) * mm, "end": v(-1798.09, -295.9) * mm});
            skLineSegment(sketch, "E138", {"start": v(-1752.05, -323.9) * mm, "end": v(-1752.05, -335.9) * mm});
            skLineSegment(sketch, "E139", {"start": v(-1752.05, -323.9) * mm, "end": v(-1746.05, -323.9) * mm});
            skSolve(sketch);
        }
        {
            var Q0;
            Q0=makeQuery(id+"F0.imprint","IMPRINT",FACE,{"disambiguationData":[TD([[makeQuery(id+"F0.imprint","IMPRINT",EDGE,{"derivedFrom":sQuery(id+"F0.wireOp",EDGE,"E68.0.1.0")}),1.0]])]});
            extrude(context, id + "F1", {"entities" : qUnion([Q0]), "depth" : 6 * mm, "offsetDistance" : 25 * mm});
        }
        {
            var Q0;
            Q0=qCreatedBy(makeId("Top.planeOp"),FACE);
            var sketch = newSketch(context, id + "F2", { "sketchPlane" : qUnion([Q0])});
            skLineSegment(sketch, "E140", {"start": v(-419.45, -61.7) * mm, "end": v(-419.45, -55.7) * mm});
            skLineSegment(sketch, "E141", {"start": v(-419.45, -55.7) * mm, "end": v(-407.45, -55.7) * mm});
            skLineSegment(sketch, "E142", {"start": v(-407.45, -55.7) * mm, "end": v(-407.45, -61.7) * mm});
            skLineSegment(sketch, "E143.1.0.0", {"start": v(-354.45, -61.7) * mm, "end": v(-354.45, -55.7) * mm});
            skLineSegment(sketch, "E143.1.0.1", {"start": v(-354.45, -55.7) * mm, "end": v(-342.45, -55.7) * mm});
            skLineSegment(sketch, "E143.1.0.2", {"start": v(-342.45, -55.7) * mm, "end": v(-342.45, -61.7) * mm});
            skLineSegment(sketch, "E143.2.0.0", {"start": v(-289.45, -61.7) * mm, "end": v(-289.45, -55.7) * mm});
            skLineSegment(sketch, "E143.2.0.1", {"start": v(-289.45, -55.7) * mm, "end": v(-277.45, -55.7) * mm});
            skLineSegment(sketch, "E143.2.0.2", {"start": v(-277.45, -55.7) * mm, "end": v(-277.45, -61.7) * mm});
            skLineSegment(sketch, "E143.3.0.0", {"start": v(-224.45, -61.7) * mm, "end": v(-224.45, -55.7) * mm});
            skLineSegment(sketch, "E143.3.0.1", {"start": v(-224.45, -55.7) * mm, "end": v(-212.45, -55.7) * mm});
            skLineSegment(sketch, "E143.3.0.2", {"start": v(-212.45, -55.7) * mm, "end": v(-212.45, -61.7) * mm});
            skLineSegment(sketch, "E143.direction1", {"start": v(-419.45, -61.7) * mm, "end": v(-382.95, -61.7) * mm, "construction": true});
            skLineSegment(sketch, "E144", {"start": v(-419.45, -61.7) * mm, "end": v(-444.45, -61.7) * mm});
            skLineSegment(sketch, "E145", {"start": v(-224.45, -61.7) * mm, "end": v(-248.95, -61.7) * mm});
            skLineSegment(sketch, "E146", {"start": v(-289.45, -61.7) * mm, "end": v(-313.95, -61.7) * mm});
            skLineSegment(sketch, "E147", {"start": v(-354.45, -61.7) * mm, "end": v(-378.95, -61.7) * mm});
            skPoint(sketch, "E148.visualSharp", {"position": v(-444.45, -92.7) * mm});
            skLineSegment(sketch, "E149", {"start": v(-382.95, -61.7) * mm, "end": v(-382.95, -66.7) * mm});
            skLineSegment(sketch, "E150", {"start": v(-382.95, -66.7) * mm, "end": v(-384.45, -66.7) * mm});
            skLineSegment(sketch, "E151", {"start": v(-384.45, -66.7) * mm, "end": v(-384.45, -70.2) * mm});
            skLineSegment(sketch, "E152", {"start": v(-384.45, -70.2) * mm, "end": v(-382.95, -70.2) * mm});
            skLineSegment(sketch, "E153", {"start": v(-382.95, -70.2) * mm, "end": v(-382.95, -73.2) * mm});
            skLineSegment(sketch, "E154", {"start": v(-382.95, -73.2) * mm, "end": v(-378.95, -73.2) * mm});
            skLineSegment(sketch, "E155", {"start": v(-378.95, -73.2) * mm, "end": v(-378.95, -70.2) * mm});
            skLineSegment(sketch, "E156", {"start": v(-378.95, -70.2) * mm, "end": v(-377.45, -70.2) * mm});
            skLineSegment(sketch, "E157", {"start": v(-377.45, -70.2) * mm, "end": v(-377.45, -66.7) * mm});
            skLineSegment(sketch, "E158", {"start": v(-377.45, -66.7) * mm, "end": v(-378.95, -66.7) * mm});
            skLineSegment(sketch, "E159", {"start": v(-378.95, -66.7) * mm, "end": v(-378.95, -61.7) * mm});
            skLineSegment(sketch, "E160.trimOffspring", {"start": v(-378.95, -61.7) * mm, "end": v(-354.45, -61.7) * mm, "construction": true});
            skLineSegment(sketch, "E161.trimOffspring", {"start": v(-382.95, -61.7) * mm, "end": v(-407.45, -61.7) * mm});
            skLineSegment(sketch, "E162", {"start": v(-317.95, -61.7) * mm, "end": v(-317.95, -66.7) * mm});
            skLineSegment(sketch, "E163", {"start": v(-317.95, -66.7) * mm, "end": v(-319.45, -66.7) * mm});
            skLineSegment(sketch, "E164", {"start": v(-319.45, -66.7) * mm, "end": v(-319.45, -70.2) * mm});
            skLineSegment(sketch, "E165", {"start": v(-319.45, -70.2) * mm, "end": v(-317.95, -70.2) * mm});
            skLineSegment(sketch, "E166", {"start": v(-317.95, -70.2) * mm, "end": v(-317.95, -73.2) * mm});
            skLineSegment(sketch, "E167", {"start": v(-317.95, -73.2) * mm, "end": v(-313.95, -73.2) * mm});
            skLineSegment(sketch, "E168", {"start": v(-313.95, -73.2) * mm, "end": v(-313.95, -70.2) * mm});
            skLineSegment(sketch, "E169", {"start": v(-313.95, -70.2) * mm, "end": v(-312.45, -70.2) * mm});
            skLineSegment(sketch, "E170", {"start": v(-312.45, -70.2) * mm, "end": v(-312.45, -66.7) * mm});
            skLineSegment(sketch, "E171", {"start": v(-312.45, -66.7) * mm, "end": v(-313.95, -66.7) * mm});
            skLineSegment(sketch, "E172", {"start": v(-313.95, -66.7) * mm, "end": v(-313.95, -61.7) * mm});
            skLineSegment(sketch, "E173.trimOffspring", {"start": v(-317.95, -61.7) * mm, "end": v(-342.45, -61.7) * mm});
            skLineSegment(sketch, "E174", {"start": v(-252.95, -61.7) * mm, "end": v(-252.95, -66.7) * mm});
            skLineSegment(sketch, "E175", {"start": v(-252.95, -66.7) * mm, "end": v(-254.45, -66.7) * mm});
            skLineSegment(sketch, "E176", {"start": v(-254.45, -66.7) * mm, "end": v(-254.45, -70.2) * mm});
            skLineSegment(sketch, "E177", {"start": v(-254.45, -70.2) * mm, "end": v(-252.95, -70.2) * mm});
            skLineSegment(sketch, "E178", {"start": v(-252.95, -70.2) * mm, "end": v(-252.95, -73.2) * mm});
            skLineSegment(sketch, "E179", {"start": v(-252.95, -73.2) * mm, "end": v(-248.95, -73.2) * mm});
            skLineSegment(sketch, "E180", {"start": v(-248.95, -73.2) * mm, "end": v(-248.95, -70.2) * mm});
            skLineSegment(sketch, "E181", {"start": v(-248.95, -70.2) * mm, "end": v(-247.45, -70.2) * mm});
            skLineSegment(sketch, "E182", {"start": v(-247.45, -70.2) * mm, "end": v(-247.45, -66.7) * mm});
            skLineSegment(sketch, "E183", {"start": v(-247.45, -66.7) * mm, "end": v(-248.95, -66.7) * mm});
            skLineSegment(sketch, "E184", {"start": v(-248.95, -66.7) * mm, "end": v(-248.95, -61.7) * mm});
            skLineSegment(sketch, "E185.trimOffspring", {"start": v(-252.95, -61.7) * mm, "end": v(-277.45, -61.7) * mm});
            skLineSegment(sketch, "E186", {"start": v(-444.45, -61.7) * mm, "end": v(-444.45, -71.27) * mm});
            skArc(sketch, "E187.filletArc", {"start": v(-444.45, -71.27) * mm, "mid": v(-438.1, -85.89) * mm, "end": v(-423.08, -91.22) * mm});
            skLineSegment(sketch, "E188", {"start": v(-212.45, -61.7) * mm, "end": v(-187.95, -61.7) * mm});
            skLineSegment(sketch, "E189", {"start": v(-187.95, -61.7) * mm, "end": v(-187.95, -66.7) * mm});
            skLineSegment(sketch, "E190", {"start": v(-187.95, -66.7) * mm, "end": v(-189.45, -66.7) * mm});
            skLineSegment(sketch, "E191", {"start": v(-189.45, -66.7) * mm, "end": v(-189.45, -70.2) * mm});
            skLineSegment(sketch, "E192", {"start": v(-189.45, -70.2) * mm, "end": v(-187.95, -70.2) * mm});
            skLineSegment(sketch, "E193", {"start": v(-187.95, -70.2) * mm, "end": v(-187.95, -73.2) * mm});
            skLineSegment(sketch, "E194", {"start": v(-187.95, -73.2) * mm, "end": v(-183.95, -73.2) * mm});
            skLineSegment(sketch, "E195", {"start": v(-183.95, -73.2) * mm, "end": v(-183.95, -70.2) * mm});
            skLineSegment(sketch, "E196", {"start": v(-183.95, -70.2) * mm, "end": v(-182.45, -70.2) * mm});
            skLineSegment(sketch, "E197", {"start": v(-182.45, -70.2) * mm, "end": v(-182.45, -66.7) * mm});
            skLineSegment(sketch, "E198", {"start": v(-182.45, -66.7) * mm, "end": v(-183.95, -66.7) * mm});
            skLineSegment(sketch, "E199", {"start": v(-183.95, -66.7) * mm, "end": v(-183.95, -61.7) * mm});
            skLineSegment(sketch, "E200.trimOffspring", {"start": v(-183.95, -61.7) * mm, "end": v(-159.45, -61.7) * mm});
            skLineSegment(sketch, "E201.0.4.0", {"start": v(-159.45, -61.7) * mm, "end": v(-159.45, -55.7) * mm});
            skLineSegment(sketch, "E201.3.4.0", {"start": v(-159.45, -55.7) * mm, "end": v(-147.45, -55.7) * mm});
            skLineSegment(sketch, "E201.6.4.0", {"start": v(-147.45, -55.7) * mm, "end": v(-147.45, -61.7) * mm});
            skLineSegment(sketch, "E202", {"start": v(-147.45, -61.7) * mm, "end": v(-142.45, -61.7) * mm});
            skLineSegment(sketch, "E203", {"start": v(-142.45, -61.7) * mm, "end": v(-142.45, -67.2) * mm});
            skLineSegment(sketch, "E204", {"start": v(-151.93, -77.18) * mm, "end": v(-423.08, -91.22) * mm});
            skPoint(sketch, "E205.visualSharp", {"position": v(-142.45, -76.7) * mm});
            skArc(sketch, "E205.filletArc", {"start": v(-151.93, -77.18) * mm, "mid": v(-145.2, -74.08) * mm, "end": v(-142.45, -67.2) * mm});
            skSolve(sketch);
        }
        {
            var Q0;
            Q0=makeQuery(id+"F2.imprint","IMPRINT",FACE,{"disambiguationData":[TD([[makeQuery(id+"F2.imprint","IMPRINT",EDGE,{"derivedFrom":sQuery(id+"F2.wireOp",EDGE,"E140")}),-1.0]])]});
            extrude(context, id + "F3", {"entities" : qUnion([Q0]), "depth" : 6 * mm, "offsetDistance" : 25 * mm});
        }
        {
            var Q0;
            Q0=qCreatedBy(makeId("Top.planeOp"),FACE);
            var sketch = newSketch(context, id + "F4", { "sketchPlane" : qUnion([Q0])});
            skLineSegment(sketch, "E206.bottom", {"start": v(356.28, 137.16) * mm, "end": v(626.28, 137.16) * mm});
            skLineSegment(sketch, "E206.top", {"start": v(356.28, -132.84) * mm, "end": v(626.28, -132.84) * mm});
            skLineSegment(sketch, "E206.left", {"start": v(356.28, 137.16) * mm, "end": v(356.28, -132.84) * mm});
            skLineSegment(sketch, "E206.right", {"start": v(626.28, 137.16) * mm, "end": v(626.28, -132.84) * mm});
            skCircle(sketch, "E207", {"center": v(361.28, 132.16) * mm, "radius": 2.15 * mm});
            skCircle(sketch, "E208", {"center": v(621.28, 132.16) * mm, "radius": 2.15 * mm});
            skCircle(sketch, "E209", {"center": v(361.28, -127.84) * mm, "radius": 2.15 * mm});
            skCircle(sketch, "E210", {"center": v(621.28, -127.84) * mm, "radius": 2.15 * mm});
            skSolve(sketch);
        }
        {
            var Q0;
            Q0=makeQuery(id+"F4.imprint","IMPRINT",FACE,{"disambiguationData":[TD([[makeQuery(id+"F4.imprint","IMPRINT",EDGE,{"derivedFrom":sQuery(id+"F4.wireOp",EDGE,"E206.bottom")}),-1.0]])]});
            extrude(context, id + "F5", {"entities" : qUnion([Q0]), "depth" : 3 * mm, "offsetDistance" : 25 * mm});
        }
    });
